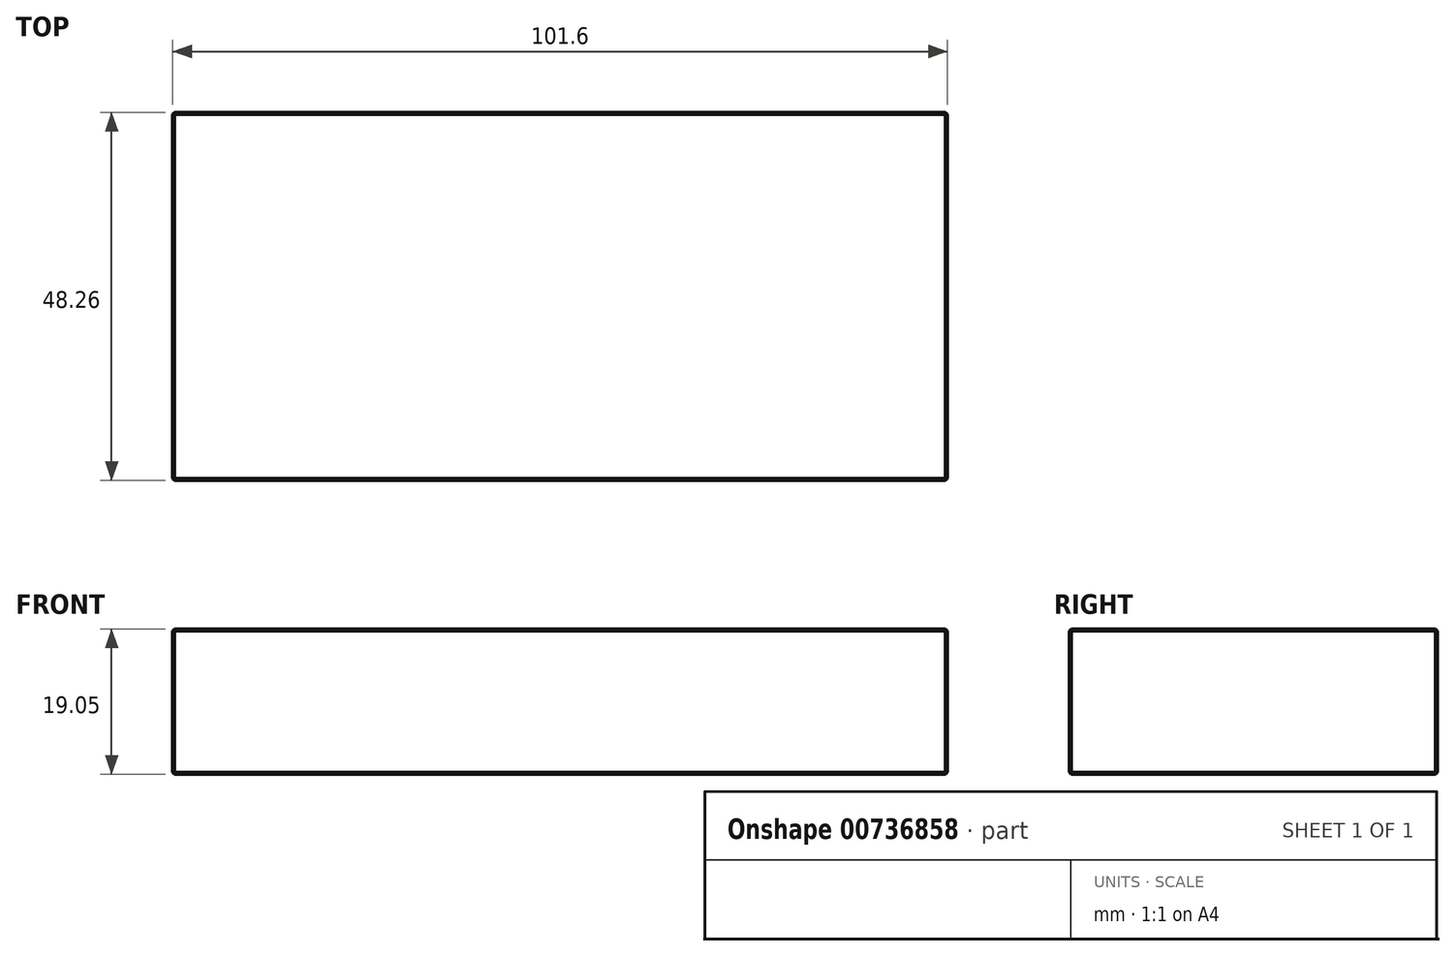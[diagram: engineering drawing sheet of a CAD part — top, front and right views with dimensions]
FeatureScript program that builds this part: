
annotation { "Feature Type Name" : "Feature", "Feature Type Description" : "" }
export const myFeature = defineFeature(function(context is Context, id is Id, definition is map)
    precondition{}
    {
        {
            var Q0;
            Q0=qCreatedBy(makeId("Top.planeOp"),FACE);
            var sketch = newSketch(context, id + "F0", { "sketchPlane" : qUnion([Q0])});
            skLineSegment(sketch, "E0.bottom", {"start": v(0, 0) * mm, "end": v(101.6, 0) * mm});
            skLineSegment(sketch, "E0.top", {"start": v(0, 48.26) * mm, "end": v(101.6, 48.26) * mm});
            skLineSegment(sketch, "E0.left", {"start": v(0, 0) * mm, "end": v(0, 48.26) * mm});
            skLineSegment(sketch, "E0.right", {"start": v(101.6, 0) * mm, "end": v(101.6, 48.26) * mm});
            skSolve(sketch);
        }
        {
            var Q0;
            Q0=makeQuery(id+"F0.imprint","IMPRINT",FACE,{"disambiguationData":[TD([[makeQuery(id+"F0.imprint","IMPRINT",EDGE,{"derivedFrom":sQuery(id+"F0.wireOp",EDGE,"E0.bottom")}),1.0]])]});
            extrude(context, id + "F1", {"entities" : qUnion([Q0]), "depth" : 19.05 * mm, "offsetDistance" : 25.4 * mm});
        }
        {
            var Q0;
            Q0=makeQuery(id+"F1.opExtrude","CAP_EDGE",EDGE,{"disambiguationData":[OSD([sQuery(id+"F0.wireOp",EDGE,"E0.left")])],"isStart":false});
            var Q1;
            Q1=makeQuery(id+"F1.opExtrude","CAP_EDGE",EDGE,{"disambiguationData":[OSD([sQuery(id+"F0.wireOp",EDGE,"E0.bottom")])],"isStart":false});
            var Q2;
            Q2=makeQuery(id+"F1.opExtrude","CAP_EDGE",EDGE,{"disambiguationData":[OSD([sQuery(id+"F0.wireOp",EDGE,"E0.right")])],"isStart":false});
            var Q3;
            Q3=makeQuery(id+"F1.opExtrude","CAP_EDGE",EDGE,{"disambiguationData":[OSD([sQuery(id+"F0.wireOp",EDGE,"E0.top")])],"isStart":false});
            var Q4;
            Q4=makeQuery(id+"F1.opExtrude","SWEPT_EDGE",EDGE,{"disambiguationData":[OSD([sQuery(id+"F0.wireOp",EDGE,"E0.top"),sQuery(id+"F0.wireOp",EDGE,"E0.right")])]});
            var Q5;
            Q5=makeQuery(id+"F1.opExtrude","CAP_EDGE",EDGE,{"disambiguationData":[OSD([sQuery(id+"F0.wireOp",EDGE,"E0.right")])],"isStart":true});
            var Q6;
            Q6=makeQuery(id+"F1.opExtrude","SWEPT_EDGE",EDGE,{"disambiguationData":[OSD([sQuery(id+"F0.wireOp",EDGE,"E0.bottom"),sQuery(id+"F0.wireOp",EDGE,"E0.right")])]});
            var Q7;
            Q7=makeQuery(id+"F1.opExtrude","CAP_EDGE",EDGE,{"disambiguationData":[OSD([sQuery(id+"F0.wireOp",EDGE,"E0.bottom")])],"isStart":true});
            var Q8;
            Q8=makeQuery(id+"F1.opExtrude","SWEPT_FACE",FACE,{"disambiguationData":[OSD([sQuery(id+"F0.wireOp",EDGE,"E0.left")])]});
            var Q9;
            Q9=makeQuery(id+"F1.opExtrude","CAP_EDGE",EDGE,{"disambiguationData":[OSD([sQuery(id+"F0.wireOp",EDGE,"E0.top")])],"isStart":true});
            var Q10;
            Q10=makeQuery(id+"F1.opExtrude","SWEPT_EDGE",EDGE,{"disambiguationData":[OSD([sQuery(id+"F0.wireOp",EDGE,"E0.top"),sQuery(id+"F0.wireOp",EDGE,"E0.left")])]});
            var Q11;
            Q11=makeQuery(id+"F1.opExtrude","CAP_EDGE",EDGE,{"disambiguationData":[OSD([sQuery(id+"F0.wireOp",EDGE,"E0.left")])],"isStart":true});
            chamfer(context, id + "F2", {"entities" : qUnion([Q0, Q1, Q2, Q3, Q4, Q5, Q6, Q7, Q8, Q9, Q10, Q11]), "width" : 0.25 * mm, "tangentPropagation" : true});
        }
    });
